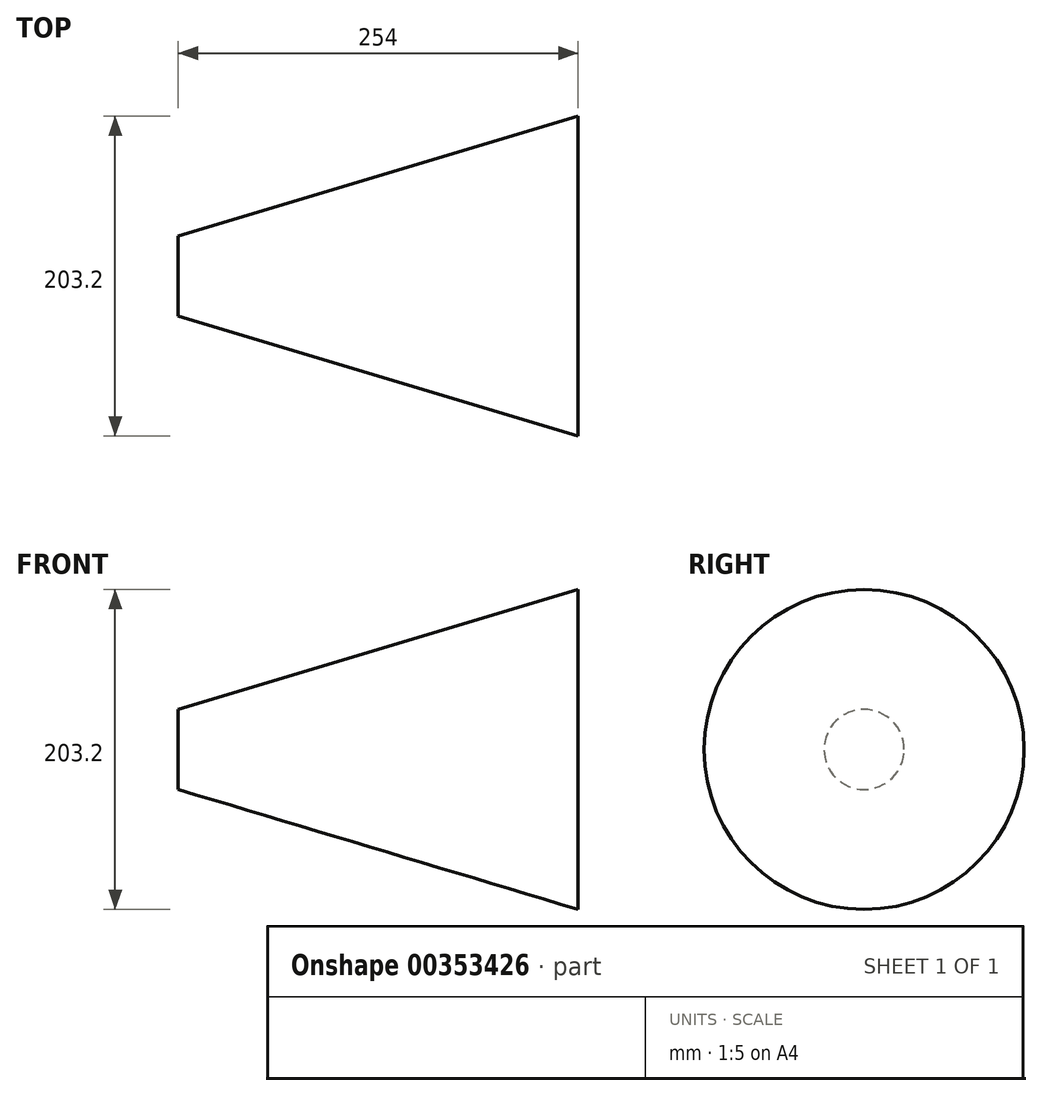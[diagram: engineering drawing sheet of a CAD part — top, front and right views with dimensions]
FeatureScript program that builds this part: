
annotation { "Feature Type Name" : "Feature", "Feature Type Description" : "" }
export const myFeature = defineFeature(function(context is Context, id is Id, definition is map)
    precondition{}
    {
        {
            var Q0;
            Q0=qCreatedBy(makeId("Right.planeOp"),FACE);
            var sketch = newSketch(context, id + "F0", { "sketchPlane" : qUnion([Q0])});
            skCircle(sketch, "E0", {"center": v(0, 0) * mm, "radius": 101.6 * mm});
            skSolve(sketch);
        }
        {
            var Q0;
            Q0=qCreatedBy(makeId("Top.planeOp"),FACE);
            var sketch = newSketch(context, id + "F1", { "sketchPlane" : qUnion([Q0])});
            skLineSegment(sketch, "E1", {"start": v(0, 0) * mm, "end": v(-254, 0) * mm});
            skLineSegment(sketch, "E2", {"start": v(0, 0) * mm, "end": v(0, -101.6) * mm});
            skLineSegment(sketch, "E3", {"start": v(-254, 0) * mm, "end": v(-254, -25.4) * mm});
            skLineSegment(sketch, "E4", {"start": v(-254, -25.4) * mm, "end": v(0, -101.6) * mm});
            skSolve(sketch);
        }
        {
            var Q0;
            Q0=makeQuery(id+"F1.imprint","IMPRINT",FACE,{"disambiguationData":[TD([[makeQuery(id+"F1.imprint","IMPRINT",EDGE,{"derivedFrom":sQuery(id+"F1.wireOp",EDGE,"E1")}),1.0]])]});
            var Q1;
            Q1=sQuery(id+"F1.wireOp",EDGE,"E1");
            revolve(context, id + "F2", {"entities" : qUnion([Q0]), "axis" : qUnion([Q1]), "revolveType" : RevolveType.FULL});
        }
    });
